# Revit family: OLDIS_ConceptEasyBox_A5879_BIM_GB
name_source: partatom
category: Plumbing Fixtures
revit_build: Autodesk Revit MEP 2012 (Build: 20110309_2315(x64)
units: mm (PartAtom-declared; Revit-internal decimal feet)

## types (1)
- A5879AA - Concept Easybox Slim Built-in Thermostatic Bath Shower Mixer Round Faceplate
    AreaUnits = millimeters
    Assembly Code = C1030200
    AssetType = Fixed
    BIMObjectName = ISI_IdealStandard_ShowerMixers_ConceptEasyBox_A5879
    BREEAM = No
    BarCode = 4015413330213
    Brand = Ideal Standard
    ConnectionType = Plumbing
    Default Elevation = 1100 mm
    Description = Concept easybox slim built-in thermostatic bath shower mixer round faceplate
    DurationUnit = year
    ECA = No
    ExpectedLife = 30
    FaucetFunction = MIXED
    FaucetOperation = Other
    FaucetTopDescription = Handwheels
    FaucetType = Other
    Features = Slim built-in thermostatic bath shower mixer round faceplate
    Finish = Chrome
    IfcExportAs = IfcValveType
    IfcExportType = FAUCET
    InstallationDate = 1900-12-31T23:59:59
    InstallationInstructions = www.idealspec.co.uk/resources.html
    LinearUnits = millimeters
    ManufacturerURL = www.idealspec.co.uk
    Model = A5879AA
    ModelNumber = A5879AA
    ModelReference = Concept easybox slim built-in thermostatic bath shower mixer round faceplate
    NBSDescription = Shower mixers
    NBSReference = 45-35-70/335
    Name = ShowerMixers_ConceptEasyBox_A5879_IdealStandard
    NettWeight = 3 Kg
    NominalHeight = 164 mm  [stored 0.538058 ft]
    NominalLength = 185 mm  [stored 0.606955 ft]
    NominalWidth = 185 mm  [stored 0.606955 ft]
    ProductInformation = www.idealspec.co.uk/assets/datasheet/A5879AA
    Shape = Sculptured
    Size = 164 x 185 x 185 mm
    Space = Internal
    SpareParts = www.fastpart-spares.co.uk
    SustainabilityPerformance = Can be recycled
    TMV3 = No
    TestPressure = 10 Bar
    URL = www.idealspec.co.uk
    Uniclass2 = Pr_40_20_87_81
    Version = 1
    VolumeUnits = Litres
    WRAS = No
    WarrantyDescription = Manufacturers warranty
    WarrantyDurationParts = 5
    WarrantyDurationUnit = year
    WarrantyStartDate = 1900-12-31T23:59:59
    WaterEfficientProduct = No

note: [stored X ft] marks values corroborated as IEEE doubles in the binary element streams (Revit-internal decimal feet)

## geometry (parser evidence)
native form markers: Sweep x2
no freeform markers — native parametric forms only
